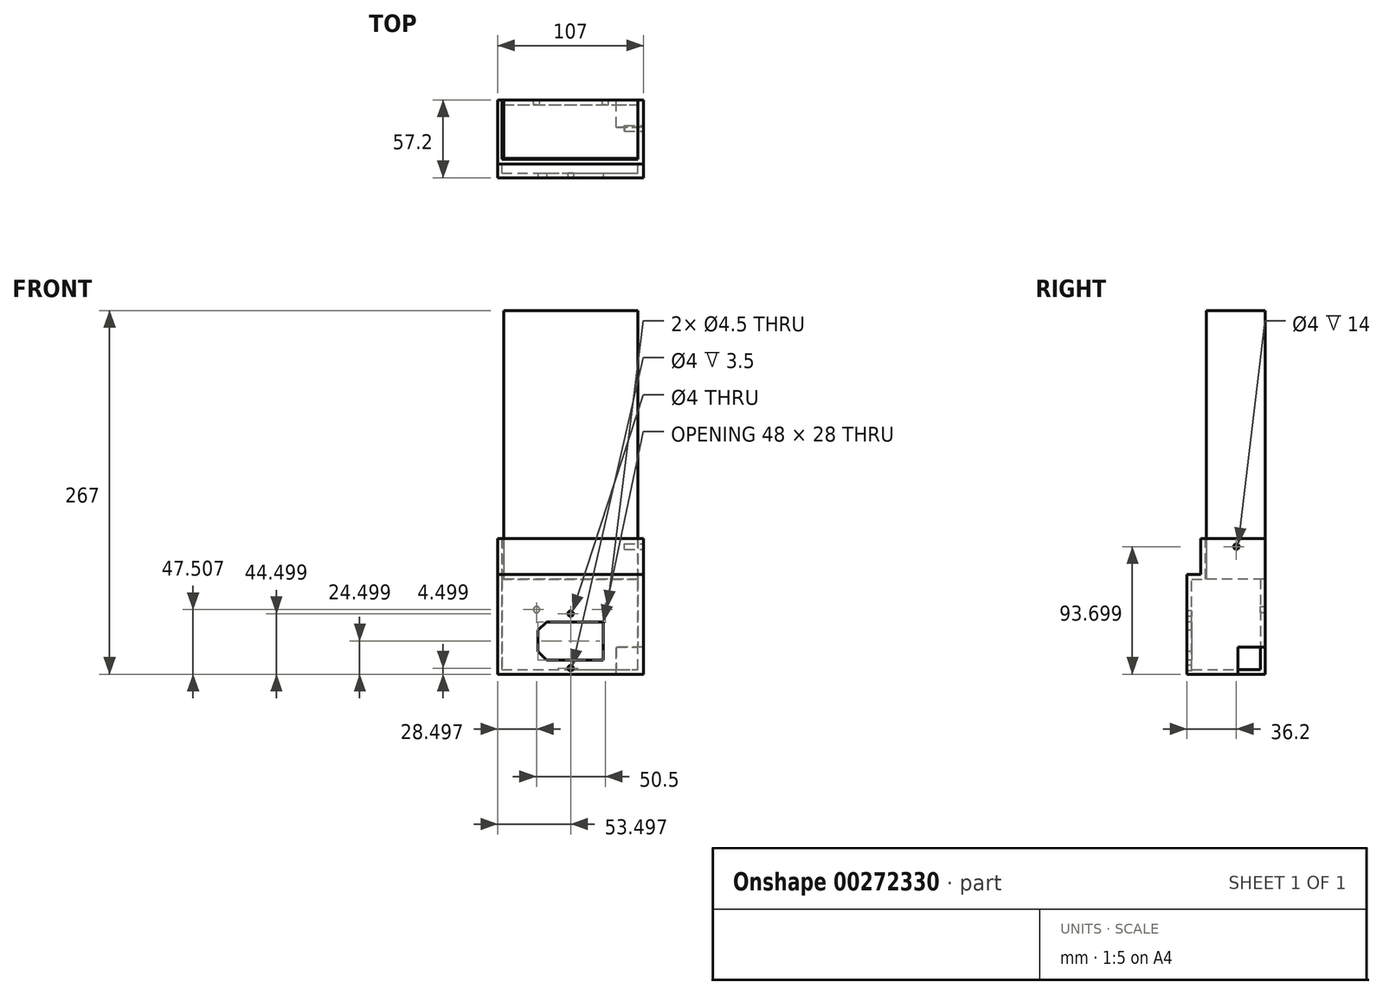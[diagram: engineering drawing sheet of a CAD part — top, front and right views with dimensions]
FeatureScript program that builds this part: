
annotation { "Feature Type Name" : "Feature", "Feature Type Description" : "" }
export const myFeature = defineFeature(function(context is Context, id is Id, definition is map)
    precondition{}
    {
        {
            var Q0;
            Q0=qCreatedBy(makeId("Front.planeOp"),FACE);
            var sketch = newSketch(context, id + "F0", { "sketchPlane" : qUnion([Q0])});
            skLineSegment(sketch, "E0.bottom", {"start": v(-59.6, 126.13) * mm, "end": v(38.9, 126.13) * mm});
            skLineSegment(sketch, "E0.top", {"start": v(-59.6, -70.87) * mm, "end": v(38.9, -70.87) * mm});
            skLineSegment(sketch, "E0.left", {"start": v(-59.6, 126.13) * mm, "end": v(-59.6, -70.87) * mm});
            skLineSegment(sketch, "E0.right", {"start": v(38.9, 126.13) * mm, "end": v(38.9, -70.87) * mm});
            skSolve(sketch);
        }
        {
            var Q0;
            Q0=makeQuery(id+"F0.imprint","IMPRINT",FACE,{"disambiguationData":[TD([[makeQuery(id+"F0.imprint","IMPRINT",EDGE,{"derivedFrom":sQuery(id+"F0.wireOp",EDGE,"E0.bottom")}),-1.0]])]});
            extrude(context, id + "F1", {"entities" : qUnion([Q0]), "depth" : 43 * mm});
        }
        {
            var Q0;
            Q0=makeQuery(id+"F1.opExtrude","SWEPT_FACE",FACE,{"disambiguationData":[OSD([sQuery(id+"F0.wireOp",EDGE,"E0.right")])]});
            var sketch = newSketch(context, id + "F2", { "sketchPlane" : qUnion([Q0])});
            skCircle(sketch, "E1", {"center": v(-21, -47.17) * mm, "radius": 2 * mm});
            skSolve(sketch);
        }
        {
            var Q0;
            Q0=makeQuery(id+"F2.imprint","IMPRINT",FACE,{"disambiguationData":[TD([[makeQuery(id+"F2.imprint","IMPRINT",EDGE,{"derivedFrom":sQuery(id+"F2.wireOp",EDGE,"JZKWuPf6-PGso-EqNF-yNsx-eXrz9TnsRI6m")}),1.0]])]});
            var Q1;
            Q1=makeQuery(id+"F2.imprint","IMPRINT",FACE,{"disambiguationData":[TD([[makeQuery(id+"F2.imprint","IMPRINT",EDGE,{"derivedFrom":sQuery(id+"F2.wireOp",EDGE,"E1")}),1.0]])]});
            extrude(context, id + "F3", {"entities" : qUnion([Q0, Q1]), "operationType" : NewBodyOperationType.REMOVE, "oppositeDirection" : true, "depth" : 10 * mm});
        }
        {
            var Q0;
            Q0=makeQuery(id+"F1.opExtrude","SWEPT_FACE",FACE,{"disambiguationData":[OSD([sQuery(id+"F0.wireOp",EDGE,"E0.right")])]});
            var sketch = newSketch(context, id + "F4", { "sketchPlane" : qUnion([Q0])});
            skLineSegment(sketch, "E2.bottom", {"start": v(-47.2, -41.17) * mm, "end": v(0, -41.17) * mm});
            skLineSegment(sketch, "E2.top", {"start": v(-47.2, -140.87) * mm, "end": v(0, -140.87) * mm});
            skLineSegment(sketch, "E2.left", {"start": v(-47.2, -67.5) * mm, "end": v(-47.2, -41.17) * mm});
            skLineSegment(sketch, "E2.right", {"start": v(0, -140.87) * mm, "end": v(0, -41.17) * mm});
            skLineSegment(sketch, "E3", {"start": v(-47.2, -140.87) * mm, "end": v(-57.2, -140.87) * mm});
            skLineSegment(sketch, "E4", {"start": v(-57.2, -140.87) * mm, "end": v(-57.2, -67.5) * mm});
            skLineSegment(sketch, "E5", {"start": v(-57.2, -67.5) * mm, "end": v(-47.2, -67.5) * mm});
            skSolve(sketch);
        }
        {
            var Q0;
            {var subQ3=sQuery(id+"F4.wireOp",EDGE,"E2.bottom");Q0=makeQuery(id+"F4.imprint","IMPRINT",FACE,{"disambiguationData":[TD([[makeQuery(id+"F4.imprint","IMPRINT",EDGE,{"derivedFrom":subQ3}),-1.0]])]});}
            var Q1;
            {var subQ0=sQuery(id+"F4.wireOp",EDGE,"E2.top");Q1=makeQuery(id+"F4.imprint","IMPRINT",FACE,{"disambiguationData":[TD([[makeQuery(id+"F4.imprint","IMPRINT",EDGE,{"derivedFrom":subQ0}),1.0]])]});}
            extrude(context, id + "F5", {"entities" : qUnion([Q0, Q1]), "depth" : 4 * mm});
        }
        {
            var Q0;
            Q0=makeQuery(id+"F5.opExtrude","CAP_FACE",FACE,{"disambiguationData":[OSD([sQuery(id+"F2.wireOp",EDGE,"E1"),sQuery(id+"F4.wireOp",EDGE,"E2.bottom"),sQuery(id+"F4.wireOp",EDGE,"E2.top"),sQuery(id+"F4.wireOp",EDGE,"E2.left"),sQuery(id+"F4.wireOp",EDGE,"E2.right")])],"isStart":true});
            var sketch = newSketch(context, id + "F6", { "sketchPlane" : qUnion([Q0])});
            skLineSegment(sketch, "E6.0", {"start": v(43.7, -44.67) * mm, "end": v(3.5, -44.67) * mm});
            skLineSegment(sketch, "E6.1", {"start": v(53.7, -137.37) * mm, "end": v(3.5, -137.37) * mm});
            skLineSegment(sketch, "E6.2", {"start": v(53.7, -137.37) * mm, "end": v(53.7, -71) * mm});
            skLineSegment(sketch, "E6.3", {"start": v(3.5, -44.67) * mm, "end": v(3.5, -137.37) * mm});
            skLineSegment(sketch, "E6.4", {"start": v(53.7, -71) * mm, "end": v(43.7, -71) * mm});
            skLineSegment(sketch, "E6.5", {"start": v(43.7, -71) * mm, "end": v(43.7, -44.67) * mm});
            skLineSegment(sketch, "E7", {"start": v(43.7, -44.67) * mm, "end": v(43.7, -41.17) * mm});
            skLineSegment(sketch, "E8", {"start": v(3.5, -70.87) * mm, "end": v(0, -70.87) * mm});
            skLineSegment(sketch, "E9", {"start": v(0, -70.87) * mm, "end": v(0, -140.87) * mm});
            skLineSegment(sketch, "E10", {"start": v(0, -140.87) * mm, "end": v(57.2, -140.87) * mm});
            skLineSegment(sketch, "E11", {"start": v(57.2, -140.87) * mm, "end": v(57.2, -67.5) * mm});
            skLineSegment(sketch, "E12", {"start": v(57.2, -67.5) * mm, "end": v(47.2, -67.5) * mm});
            skLineSegment(sketch, "E13", {"start": v(47.2, -67.5) * mm, "end": v(47.2, -41.17) * mm});
            skLineSegment(sketch, "E14", {"start": v(47.2, -41.17) * mm, "end": v(43.7, -41.17) * mm});
            skSolve(sketch);
        }
        {
            var Q0;
            {var subQ1=sQuery(id+"F6.wireOp",EDGE,"E6.1");Q0=makeQuery(id+"F6.imprint","IMPRINT",FACE,{"disambiguationData":[TD([[makeQuery(id+"F6.imprint","IMPRINT",EDGE,{"derivedFrom":subQ1}),1.0]])]});}
            extrude(context, id + "F7", {"entities" : qUnion([Q0]), "operationType" : NewBodyOperationType.ADD, "depth" : 100 * mm});
        }
        {
            var Q0;
            Q0=makeQuery(id+"F7.opExtrude","CAP_FACE",FACE,{"disambiguationData":[OSD([sQuery(id+"F6.wireOp",EDGE,"E6.1"),sQuery(id+"F6.wireOp",EDGE,"E6.2"),sQuery(id+"F6.wireOp",EDGE,"E6.3"),sQuery(id+"F6.wireOp",EDGE,"E6.4"),sQuery(id+"F6.wireOp",EDGE,"E6.5"),sQuery(id+"F6.wireOp",EDGE,"E7"),sQuery(id+"F6.wireOp",EDGE,"E8"),sQuery(id+"F6.wireOp",EDGE,"E9"),sQuery(id+"F6.wireOp",EDGE,"E10"),sQuery(id+"F6.wireOp",EDGE,"E11"),sQuery(id+"F6.wireOp",EDGE,"E12"),sQuery(id+"F6.wireOp",EDGE,"E13"),sQuery(id+"F6.wireOp",EDGE,"E14")])],"isStart":false});
            var sketch = newSketch(context, id + "F8", { "sketchPlane" : qUnion([Q0])});
            skLineSegment(sketch, "E15", {"start": v(0, -140.87) * mm, "end": v(57.2, -140.87) * mm});
            skLineSegment(sketch, "E16", {"start": v(57.2, -140.87) * mm, "end": v(57.2, -67.5) * mm});
            skLineSegment(sketch, "E17", {"start": v(57.2, -67.5) * mm, "end": v(47.2, -67.5) * mm});
            skLineSegment(sketch, "E18", {"start": v(47.2, -67.5) * mm, "end": v(47.2, -41.17) * mm});
            skLineSegment(sketch, "E19", {"start": v(47.2, -41.17) * mm, "end": v(43.7, -41.17) * mm});
            skLineSegment(sketch, "E20", {"start": v(43.7, -41.17) * mm, "end": v(0, -41.17) * mm});
            skLineSegment(sketch, "E21", {"start": v(0, -41.17) * mm, "end": v(0, -140.87) * mm});
            skSolve(sketch);
        }
        {
            var Q0;
            Q0 = qSketchRegion(id + "F8", true);
            extrude(context, id + "F9", {"entities" : qUnion([Q0]), "operationType" : NewBodyOperationType.ADD, "depth" : 3 * mm});
        }
        {
            var Q0;
            Q0=makeQuery(id+"F9.boolean.opBoolean","MERGE",FACE,{"derivedFrom":[makeQuery(id+"F7.boolean.opBoolean","MERGE",FACE,{"derivedFrom":[makeQuery(id+"F5.opExtrude","SWEPT_FACE",FACE,{"disambiguationData":[OSD([sQuery(id+"F4.wireOp",EDGE,"E2.right")])]}),makeQuery(id+"F7.opExtrude","SWEPT_FACE",FACE,{"disambiguationData":[OSD([sQuery(id+"F6.wireOp",EDGE,"E9")])]})]}),makeQuery(id+"F9.opExtrude","SWEPT_FACE",FACE,{"disambiguationData":[OSD([sQuery(id+"F8.wireOp",EDGE,"E21")])]})]});
            var sketch = newSketch(context, id + "F10", { "sketchPlane" : qUnion([Q0])});
            skCircle(sketch, "E22", {"center": v(-14.9, -93.36) * mm, "radius": 2.25 * mm});
            skCircle(sketch, "E23", {"center": v(35.6, -93.36) * mm, "radius": 2.25 * mm});
            skLineSegment(sketch, "E24", {"start": v(-14.9, -93.36) * mm, "end": v(35.6, -93.36) * mm});
            skPoint(sketch, "E25", {"position": v(10.34, -93.36) * mm});
            skLineSegment(sketch, "E26", {"start": v(10.34, -93.36) * mm, "end": v(10.34, -70.87) * mm, "construction": true});
            skSolve(sketch);
        }
        {
            var Q0;
            Q0=makeQuery(id+"F10.imprint","IMPRINT",FACE,{"disambiguationData":[TD([[makeQuery(id+"F10.imprint","IMPRINT",EDGE,{"derivedFrom":sQuery(id+"F10.wireOp",EDGE,"E22")}),1.0]])]});
            var Q1;
            Q1=makeQuery(id+"F10.imprint","IMPRINT",FACE,{"disambiguationData":[TD([[makeQuery(id+"F10.imprint","IMPRINT",EDGE,{"derivedFrom":sQuery(id+"F10.wireOp",EDGE,"E23")}),1.0]])]});
            var Q2;
            Q2=makeQuery(id+"F7.opExtrude","SWEPT_FACE",FACE,{"disambiguationData":[OSD([sQuery(id+"F6.wireOp",EDGE,"E6.3")])]});
            extrude(context, id + "F11", {"entities" : qUnion([Q0, Q1]), "operationType" : NewBodyOperationType.REMOVE, "endBound" : BoundingType.UP_TO_SURFACE, "oppositeDirection" : true, "endBoundEntityFace" : qUnion([Q2]), "depth" : 25 * mm});
        }
        {
            var Q0;
            Q0=makeQuery(id+"F9.boolean.opBoolean","MERGE",FACE,{"derivedFrom":[makeQuery(id+"F7.boolean.opBoolean","MERGE",FACE,{"derivedFrom":[makeQuery(id+"F5.opExtrude","SWEPT_FACE",FACE,{"disambiguationData":[OSD([sQuery(id+"F4.wireOp",EDGE,"E4")])]}),makeQuery(id+"F7.opExtrude","SWEPT_FACE",FACE,{"disambiguationData":[OSD([sQuery(id+"F6.wireOp",EDGE,"E11")])]})]}),makeQuery(id+"F9.opExtrude","SWEPT_FACE",FACE,{"disambiguationData":[OSD([sQuery(id+"F8.wireOp",EDGE,"E16")])]})]});
            var sketch = newSketch(context, id + "F12", { "sketchPlane" : qUnion([Q0])});
            skLineSegment(sketch, "E27", {"start": v(-10.6, -91.87) * mm, "end": v(-10.6, -140.87) * mm, "construction": true});
            skLineSegment(sketch, "E28", {"start": v(-40.1, -103.37) * mm, "end": v(-40.1, -129.37) * mm});
            skLineSegment(sketch, "E29", {"start": v(18.9, -103.37) * mm, "end": v(18.9, -129.37) * mm});
            skLineSegment(sketch, "E30", {"start": v(-40.1, -103.37) * mm, "end": v(-10.6, -91.87) * mm});
            skLineSegment(sketch, "E31", {"start": v(-10.6, -91.87) * mm, "end": v(18.9, -103.37) * mm});
            skLineSegment(sketch, "E32", {"start": v(18.9, -129.37) * mm, "end": v(-10.6, -140.87) * mm});
            skLineSegment(sketch, "E33", {"start": v(-10.6, -140.87) * mm, "end": v(-40.1, -129.37) * mm});
            skLineSegment(sketch, "E34", {"start": v(-40.1, -116.37) * mm, "end": v(18.9, -116.37) * mm, "construction": true});
            skCircle(sketch, "E35", {"center": v(-10.6, -96.37) * mm, "radius": 2 * mm});
            skCircle(sketch, "E36", {"center": v(-10.6, -136.37) * mm, "radius": 2 * mm});
            skLineSegment(sketch, "E37", {"start": v(-10.6, -96.37) * mm, "end": v(-10.6, -136.37) * mm, "construction": true});
            skPoint(sketch, "E38", {"position": v(-10.6, -116.37) * mm});
            skLineSegment(sketch, "E39.bottom", {"start": v(-28.1, -102.87) * mm, "end": v(12.9, -102.87) * mm});
            skLineSegment(sketch, "E39.top", {"start": v(-28.1, -129.87) * mm, "end": v(12.9, -129.87) * mm});
            skLineSegment(sketch, "E39.right", {"start": v(12.9, -102.87) * mm, "end": v(12.9, -129.87) * mm});
            skLineSegment(sketch, "E40", {"start": v(-34.1, -108.87) * mm, "end": v(-34.1, -123.87) * mm});
            skLineSegment(sketch, "E41", {"start": v(-34.1, -123.87) * mm, "end": v(-28.1, -129.87) * mm});
            skLineSegment(sketch, "E42", {"start": v(-34.1, -108.87) * mm, "end": v(-28.1, -102.87) * mm});
            skLineSegment(sketch, "E43", {"start": v(12.9, -116.37) * mm, "end": v(-34.1, -116.37) * mm, "construction": true});
            skPoint(sketch, "E43.endSnap0", {"position": v(12.9, -116.37) * mm});
            skLineSegment(sketch, "E44", {"start": v(-28.1, -102.87) * mm, "end": v(-28.1, -129.87) * mm, "construction": true});
            skLineSegment(sketch, "E45.0", {"start": v(-34.6, -108.66) * mm, "end": v(-34.6, -124.08) * mm});
            skLineSegment(sketch, "E45.1", {"start": v(-28.3, -102.37) * mm, "end": v(13.4, -102.37) * mm});
            skLineSegment(sketch, "E45.2", {"start": v(13.4, -102.37) * mm, "end": v(13.4, -130.37) * mm});
            skLineSegment(sketch, "E45.3", {"start": v(-34.6, -108.66) * mm, "end": v(-28.3, -102.37) * mm});
            skLineSegment(sketch, "E45.4", {"start": v(-28.3, -130.37) * mm, "end": v(13.4, -130.37) * mm});
            skLineSegment(sketch, "E45.5", {"start": v(-34.6, -124.08) * mm, "end": v(-28.3, -130.37) * mm});
            skSolve(sketch);
        }
        {
            var Q0;
            Q0=makeQuery(id+"F12.imprint","IMPRINT",FACE,{"disambiguationData":[TD([[makeQuery(id+"F12.imprint","IMPRINT",EDGE,{"derivedFrom":sQuery(id+"F12.wireOp",EDGE,"E39.bottom")}),1.0]])]});
            var Q1;
            Q1=makeQuery(id+"F12.imprint","IMPRINT",FACE,{"disambiguationData":[TD([[makeQuery(id+"F12.imprint","IMPRINT",EDGE,{"derivedFrom":sQuery(id+"F12.wireOp",EDGE,"E39.bottom")}),-1.0]])]});
            var Q2;
            Q2=makeQuery(id+"F12.imprint","IMPRINT",FACE,{"disambiguationData":[TD([[makeQuery(id+"F12.imprint","IMPRINT",EDGE,{"derivedFrom":sQuery(id+"F12.wireOp",EDGE,"E36")}),1.0]])]});
            var Q3;
            Q3=makeQuery(id+"F12.imprint","IMPRINT",FACE,{"disambiguationData":[TD([[makeQuery(id+"F12.imprint","IMPRINT",EDGE,{"derivedFrom":sQuery(id+"F12.wireOp",EDGE,"E35")}),1.0]])]});
            var Q4;
            Q4=makeQuery(id+"F7.opExtrude","SWEPT_FACE",FACE,{"disambiguationData":[OSD([sQuery(id+"F6.wireOp",EDGE,"E6.2")])]});
            extrude(context, id + "F13", {"entities" : qUnion([Q0, Q1, Q2, Q3]), "operationType" : NewBodyOperationType.REMOVE, "endBound" : BoundingType.UP_TO_SURFACE, "oppositeDirection" : true, "endBoundEntityFace" : qUnion([Q4]), "depth" : 25 * mm});
        }
        {
            var Q0;
            Q0=makeQuery(id+"F9.boolean.opBoolean","MERGE",FACE,{"derivedFrom":[makeQuery(id+"F7.boolean.opBoolean","MERGE",FACE,{"derivedFrom":[makeQuery(id+"F5.opExtrude","SWEPT_FACE",FACE,{"disambiguationData":[OSD([sQuery(id+"F4.wireOp",EDGE,"E2.right")])]}),makeQuery(id+"F7.opExtrude","SWEPT_FACE",FACE,{"disambiguationData":[OSD([sQuery(id+"F6.wireOp",EDGE,"E9")])]})]}),makeQuery(id+"F9.opExtrude","SWEPT_FACE",FACE,{"disambiguationData":[OSD([sQuery(id+"F8.wireOp",EDGE,"E21")])]})]});
            var sketch = newSketch(context, id + "F14", { "sketchPlane" : qUnion([Q0])});
            skLineSegment(sketch, "E46.bottom", {"start": v(-42.9, -140.87) * mm, "end": v(-22.9, -140.87) * mm});
            skLineSegment(sketch, "E46.top", {"start": v(-42.9, -120.87) * mm, "end": v(-22.9, -120.87) * mm});
            skLineSegment(sketch, "E46.left", {"start": v(-42.9, -140.87) * mm, "end": v(-42.9, -120.87) * mm});
            skLineSegment(sketch, "E46.right", {"start": v(-22.9, -140.87) * mm, "end": v(-22.9, -120.87) * mm});
            skSolve(sketch);
        }
        {
            var Q0;
            Q0=makeQuery(id+"F14.imprint","IMPRINT",FACE,{"disambiguationData":[TD([[makeQuery(id+"F14.imprint","IMPRINT",EDGE,{"derivedFrom":sQuery(id+"F14.wireOp",EDGE,"E46.bottom")}),1.0]])]});
            extrude(context, id + "F15", {"entities" : qUnion([Q0]), "operationType" : NewBodyOperationType.REMOVE, "oppositeDirection" : true, "depth" : 20 * mm});
        }
    });
